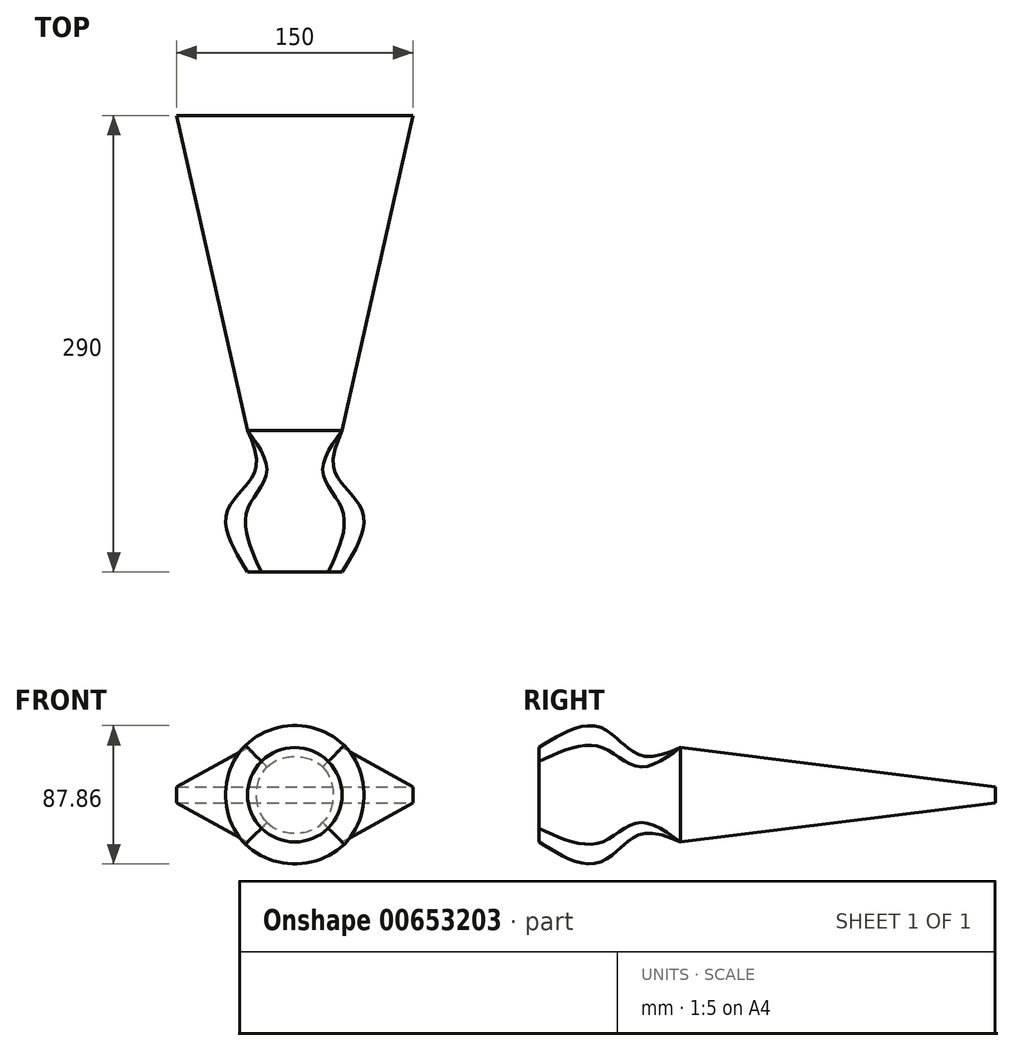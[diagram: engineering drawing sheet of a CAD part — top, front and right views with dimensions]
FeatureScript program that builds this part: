
annotation { "Feature Type Name" : "Feature", "Feature Type Description" : "" }
export const myFeature = defineFeature(function(context is Context, id is Id, definition is map)
    precondition{}
    {
        {
            var Q0;
            Q0=qCreatedBy(makeId("Front.planeOp"),FACE);
            cPlane(context, id + "F0", {"entities" : qUnion([Q0]), "cplaneType" : CPlaneType.OFFSET, "offset" : 25 * mm, "width" : 150 * mm, "height" : 150 * mm});
        }
        {
            var Q0;
            Q0=qCreatedBy(id+"F0.planeOp",FACE);
            cPlane(context, id + "F1", {"entities" : qUnion([Q0]), "cplaneType" : CPlaneType.OFFSET, "offset" : 25 * mm, "width" : 150 * mm, "height" : 150 * mm});
        }
        {
            var Q0;
            Q0=qCreatedBy(id+"F1.planeOp",FACE);
            cPlane(context, id + "F2", {"entities" : qUnion([Q0]), "cplaneType" : CPlaneType.OFFSET, "offset" : 40 * mm, "width" : 150 * mm, "height" : 150 * mm});
        }
        {
            var Q0;
            Q0=qCreatedBy(makeId("Front.planeOp"),FACE);
            var sketch = newSketch(context, id + "F3", { "sketchPlane" : qUnion([Q0])});
            skLineSegment(sketch, "E0.bottom", {"start": v(30, -30) * mm, "end": v(-30, -30) * mm});
            skLineSegment(sketch, "E0.top", {"start": v(30, 30) * mm, "end": v(-30, 30) * mm});
            skLineSegment(sketch, "E0.left", {"start": v(30, -30) * mm, "end": v(30, 30) * mm});
            skLineSegment(sketch, "E0.right", {"start": v(-30, -30) * mm, "end": v(-30, 30) * mm});
            skPoint(sketch, "E0.middle", {"position": v(0, 0) * mm});
            skSolve(sketch);
        }
        {
            var Q0;
            Q0=qCreatedBy(id+"F0.planeOp",FACE);
            var sketch = newSketch(context, id + "F4", { "sketchPlane" : qUnion([Q0])});
            skCircle(sketch, "E1", {"center": v(0, 0) * mm, "radius": 25 * mm});
            skSolve(sketch);
        }
        {
            var Q0;
            Q0=qCreatedBy(id+"F1.planeOp",FACE);
            var sketch = newSketch(context, id + "F5", { "sketchPlane" : qUnion([Q0])});
            skCircle(sketch, "E2", {"center": v(0, 0) * mm, "radius": 42.43 * mm});
            skSolve(sketch);
        }
        {
            var Q0;
            Q0=qCreatedBy(id+"F2.planeOp",FACE);
            var sketch = newSketch(context, id + "F6", { "sketchPlane" : qUnion([Q0])});
            skCircle(sketch, "E3", {"center": v(0, 0) * mm, "radius": 30 * mm});
            skSolve(sketch);
        }
        {
            var Q0;
            Q0 = qSketchRegion(id + "F3", true);
            var Q1;
            Q1 = qSketchRegion(id + "F4", true);
            var Q2;
            Q2 = qSketchRegion(id + "F5", true);
            var Q3;
            Q3 = qSketchRegion(id + "F6", true);
            loft(context, id + "F7", {"sheetProfilesArray" : [{ "sheetProfileEntities" : qUnion([Q0]) }, { "sheetProfileEntities" : qUnion([Q1]) }, { "sheetProfileEntities" : qUnion([Q2]) }, { "sheetProfileEntities" : qUnion([Q3]) }]});
        }
        {
            var Q0;
            Q0=qCreatedBy(makeId("Front.planeOp"),FACE);
            cPlane(context, id + "F8", {"entities" : qUnion([Q0]), "cplaneType" : CPlaneType.OFFSET, "offset" : 200 * mm, "oppositeDirection" : true, "width" : 150 * mm, "height" : 150 * mm});
        }
        {
            var Q0;
            Q0=qCreatedBy(id+"F8.planeOp",FACE);
            var sketch = newSketch(context, id + "F9", { "sketchPlane" : qUnion([Q0])});
            skLineSegment(sketch, "E4.bottom", {"start": v(-75, -5) * mm, "end": v(75, -5) * mm});
            skLineSegment(sketch, "E4.top", {"start": v(-75, 5) * mm, "end": v(75, 5) * mm});
            skLineSegment(sketch, "E4.left", {"start": v(-75, -5) * mm, "end": v(-75, 5) * mm});
            skLineSegment(sketch, "E4.right", {"start": v(75, -5) * mm, "end": v(75, 5) * mm});
            skPoint(sketch, "E4.middle", {"position": v(0, 0) * mm});
            skSolve(sketch);
        }
        {
            var Q1;
            Q1=makeQuery(id+"F9.imprint","IMPRINT",FACE,{"disambiguationData":[TD([[makeQuery(id+"F9.imprint","IMPRINT",EDGE,{"derivedFrom":sQuery(id+"F9.wireOp",EDGE,"E4.bottom")}),1.0]])]});
            var Q2;
            Q2=makeQuery(id+"F7.opLoft","CAP_FACE",FACE,{"disambiguationData":[OSD([makeQuery(id+"F3.imprint","IMPRINT",FACE,{"disambiguationData":[TD([[makeQuery(id+"F3.imprint","IMPRINT",EDGE,{"derivedFrom":sQuery(id+"F3.wireOp",EDGE,"E0.bottom")}),-1.0]])]})])],"isStart":true});
            loft(context, id + "F10", {"operationType" : NewBodyOperationType.ADD, "sheetProfilesArray" : [{ "sheetProfileEntities" : qUnion([Q1]) }, { "sheetProfileEntities" : qUnion([Q2]) }]});
        }
    });
